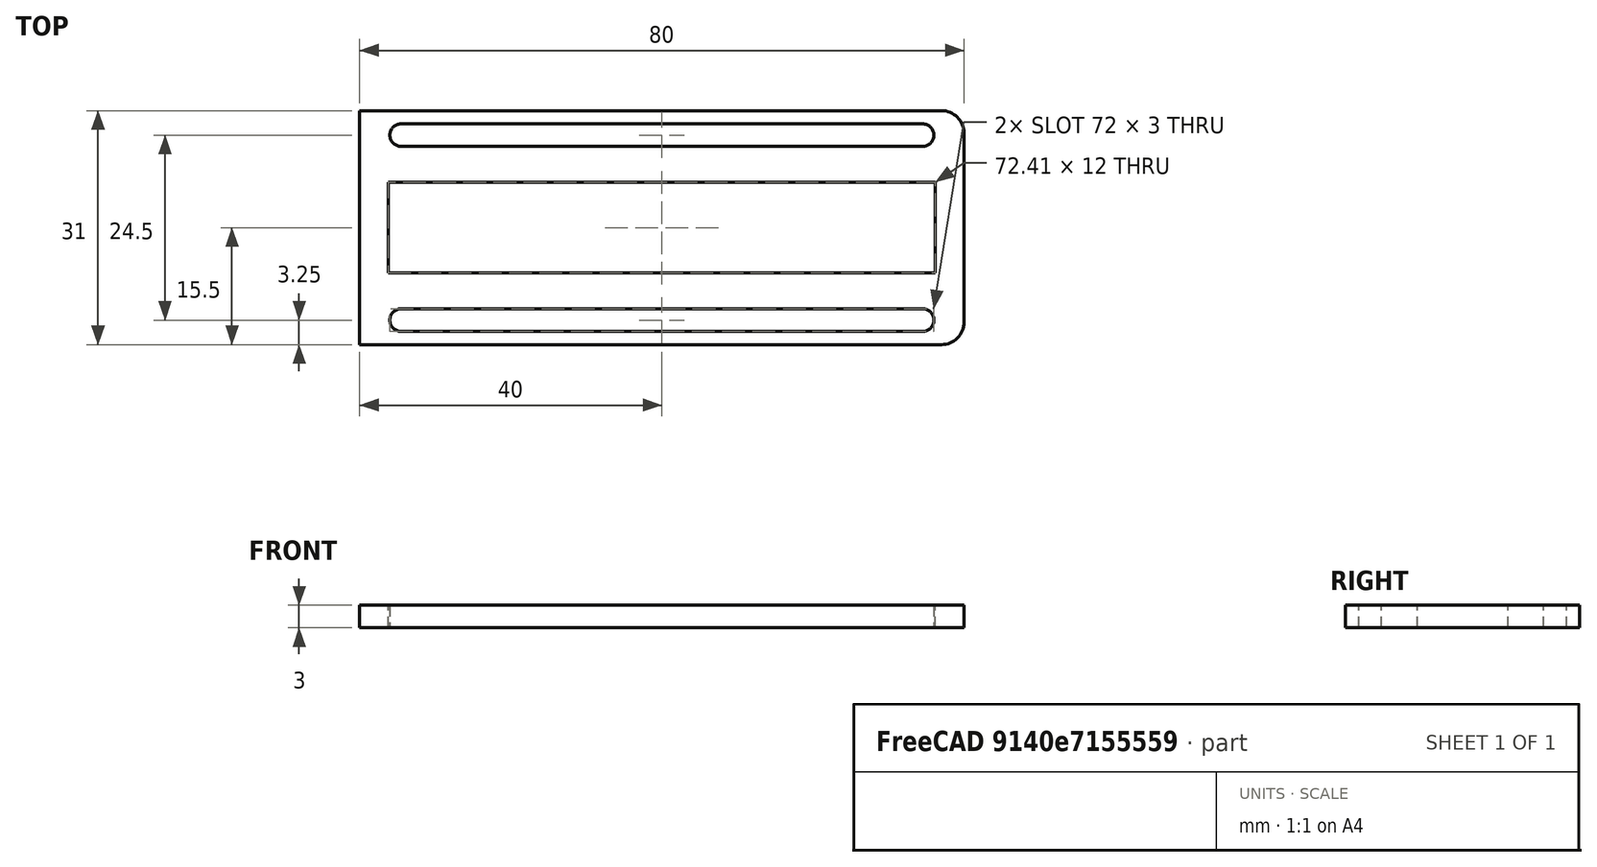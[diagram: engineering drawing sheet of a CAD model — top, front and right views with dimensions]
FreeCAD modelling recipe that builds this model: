
FCSTD DOCUMENT  (FreeCAD 0.18R4 (GitTag))
Label: Platform
License: All rights reserved
LicenseURL: http://en.wikipedia.org/wiki/All_rights_reserved
objects: Sketcher::SketchObject×1, Part::Extrusion×1, Part::Fillet×1
note: 3 computed .brp shape members not serialized (recipe doc carries the construction recipe); baked Part::Feature solids carry a one-line shape summary decoded from their .brp

FEATURE [Sketcher::SketchObject] Sketch003  label="Platform"
  sketch-geometry (16):
    g0: LineSegment StartX=-40 StartY=15.5 StartZ=0 EndX=40 EndY=15.5 EndZ=0
    g1: LineSegment StartX=40 StartY=15.5 StartZ=0 EndX=40 EndY=-15.5 EndZ=0
    g2: LineSegment StartX=40 StartY=-15.5 StartZ=0 EndX=-40 EndY=-15.5 EndZ=0
    g3: LineSegment StartX=-40 StartY=-15.5 StartZ=0 EndX=-40 EndY=15.5 EndZ=0
    g4: LineSegment StartX=-36.2042 StartY=6 StartZ=0 EndX=36.2042 EndY=6 EndZ=0
    g5: LineSegment StartX=36.2042 StartY=6 StartZ=0 EndX=36.2042 EndY=-6 EndZ=0
    g6: LineSegment StartX=36.2042 StartY=-6 StartZ=0 EndX=-36.2042 EndY=-6 EndZ=0
    g7: LineSegment StartX=-36.2042 StartY=-6 StartZ=0 EndX=-36.2042 EndY=6 EndZ=0
    g8: ArcOfCircle CenterX=-34.5 CenterY=12.25 CenterZ=0 NormalX=0 NormalY=0 NormalZ=1 AngleXU=0 Radius=1.5 StartAngle=1.5708 EndAngle=4.71239
    g9: ArcOfCircle CenterX=34.5 CenterY=12.25 CenterZ=0 NormalX=0 NormalY=0 NormalZ=1 AngleXU=0 Radius=1.5 StartAngle=4.71239 EndAngle=7.85398
    g10: LineSegment StartX=-34.5 StartY=10.75 StartZ=0 EndX=34.5 EndY=10.75 EndZ=0
    g11: LineSegment StartX=-34.5 StartY=13.75 StartZ=0 EndX=34.5 EndY=13.75 EndZ=0
    g12: ArcOfCircle CenterX=-34.5 CenterY=-12.25 CenterZ=0 NormalX=0 NormalY=0 NormalZ=1 AngleXU=0 Radius=1.5 StartAngle=1.5708 EndAngle=4.71239
    g13: ArcOfCircle CenterX=34.5 CenterY=-12.25 CenterZ=0 NormalX=0 NormalY=0 NormalZ=1 AngleXU=0 Radius=1.5 StartAngle=4.71239 EndAngle=7.85398
    g14: LineSegment StartX=-34.5 StartY=-13.75 StartZ=0 EndX=34.5 EndY=-13.75 EndZ=0
    g15: LineSegment StartX=-34.5 StartY=-10.75 StartZ=0 EndX=34.5 EndY=-10.75 EndZ=0
  constraints (36):
    c: Coincident(g0,g1)
    c: Coincident(g1,g2)
    c: Coincident(g2,g3)
    c: Coincident(g3,g0)
    c: Symmetric(g1,g0,g-1)
    c: Symmetric(g0,g0,g-2)
    c: DistanceX(g0,g0) = 80
    c: DistanceY(g1,g1) = 31
    c: Coincident(g4,g5)
    c: Coincident(g5,g6)
    c: Coincident(g6,g7)
    c: Coincident(g7,g4)
    c: Horizontal(g6)
    c: Vertical(g5)
    c: Symmetric(g2,g0,g-1)
    c: Tangent(g8,g11) = 1.5708
    c: Tangent(g8,g10) = -1.5708
    c: Tangent(g10,g9) = -1.5708
    c: Tangent(g11,g9) = 1.5708
    c: Horizontal(g10)
    c: Tangent(g12,g15) = 1.5708
    c: Tangent(g12,g14) = -1.5708
    c: Tangent(g14,g13) = -1.5708
    c: Tangent(g15,g13) = 1.5708
    c: Horizontal(g14)
    c: DistanceY(g9,g9) = 3
    c: DistanceY(g13,g13) = 3
    c: DistanceY(g13,g9) = 21.5
    c: DistanceY(g7,g7) = 12
    c: Symmetric(g4,g6,g-1)
    c: Symmetric(g4,g4,g-2)
    c: Symmetric(g8,g9,g-2)
    c: Symmetric(g12,g13,g-2)
    c: DistanceX(g11,g11) = 69
    c: DistanceX(g15,g15) = 69
    c: DistanceY(g12,g-1) = 10.75
FEATURE [Part::Extrusion] Extrude
  Base = -> Sketch003
  Dir = (0,0,1)
  DirMode = 2
  FaceMakerClass = Part::FaceMakerBullseye
  LengthFwd = 3
  LengthRev = 0
  Solid = true
  Symmetric = false
FEATURE [Part::Fillet] Fillet
  Base = -> Extrude
  Edges = 2 edges r=3: [Edge2,Edge5]
